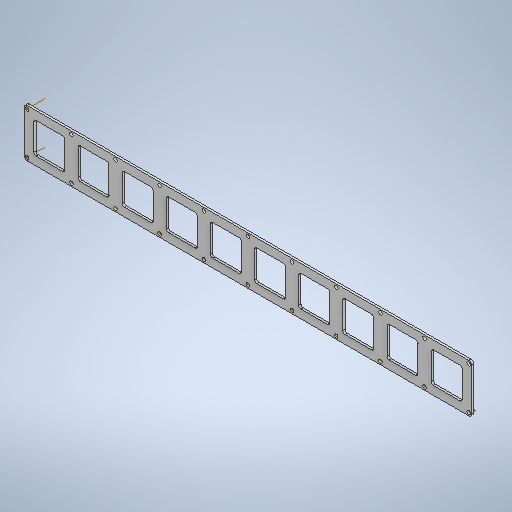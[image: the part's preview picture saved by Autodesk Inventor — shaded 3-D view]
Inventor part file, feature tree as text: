
AUTODESK INVENTOR PART (.ipt)
format: ipt  version: 2025.2 (Build 292293000, 293)  size: 407,552 bytes
history: native  units: mm
features: other x15, pattern_linear x4, extrude x2, hole x2, fillet x2, sketch x2
ambient origin geometry x8: Origin, YZ Plane, XZ Plane, XY Plane, X Axis, Y Axis, Z Axis, Center Point
bodies: Volumenkörper1 (feature_tree)
feature tree (27):
  extrude  "Extrusion1"  Depth=304.0mm
  other  "Arbeitsachse1"
  other  "Arbeitsachse2"
  extrude  "Extrusion2"  Depth=2.0mm
  pattern_linear  "Rechteckige Anordnung1"  Spacing1=2.0mm  [1 undecoded]
  other  "Arbeitspunkt1"
  hole  "Bohrung1"  [1 undecoded]
  pattern_linear  "Rechteckige Anordnung2"  Spacing1=18.0mm  [1 undecoded]
  pattern_linear  "Rechteckige Anordnung3"  Spacing1=145.0mm  [1 undecoded]
  other  "Arbeitspunkt12"
  hole  "Bohrung2"  [1 undecoded]
  pattern_linear  "Rechteckige Anordnung4"  Spacing1=21.0mm  [1 undecoded]
  fillet  "Rundung1"  Radius=21.0mm
  fillet  "Rundung2"  Radius=6.5mm
  sketch  "Skizze1"  dims[d0=90.0deg d1=32.6mm d2=304.0mm]
  sketch  "Skizze2"  dims[d3=2.0mm d4=2.0mm d5=2.0mm d6=2.0mm d7=18.0mm d8=145.0mm d9=1.5mm d10=0.0mm d11=21.0mm d12=21.0mm d13=6.5mm d14=5.8mm d15=0.0mm d16=0.0mm d17=100.0mm d19=30.0mm d20=10.0mm d21=10.0mm d22=2.4mm d23=6.0mm d24=4.0mm d25=2.0mm d26=90.0deg d27=4.2mm d28=20.594885mm d29=110.0mm d31=30.0mm d32=110.0mm d34=30.0mm d35=10.0mm d36=10.0mm d37=2.4mm d38=6.0mm d39=4.0mm d40=2.0mm d41=90.0deg d42=4.2mm d43=20.594885mm d44=110.0mm d46=30.0mm d47=1.5mm d48=1.5mm]
  other  "Arbeitspunkt2"
  other  "Arbeitspunkt3"
  other  "Arbeitspunkt4"
  other  "Arbeitspunkt5"
  other  "Arbeitspunkt6"
  other  "Arbeitspunkt7"
  other  "Arbeitspunkt8"
  other  "Arbeitspunkt9"
  other  "Arbeitspunkt10"
  other  "Arbeitspunkt11"
  other  "Arbeitsachse3"
note: 6 required parameter values undecoded (feature->parameter linkage not recoverable at this tier; creation-order binding heuristic only, values carry confidence <= 0.55)
